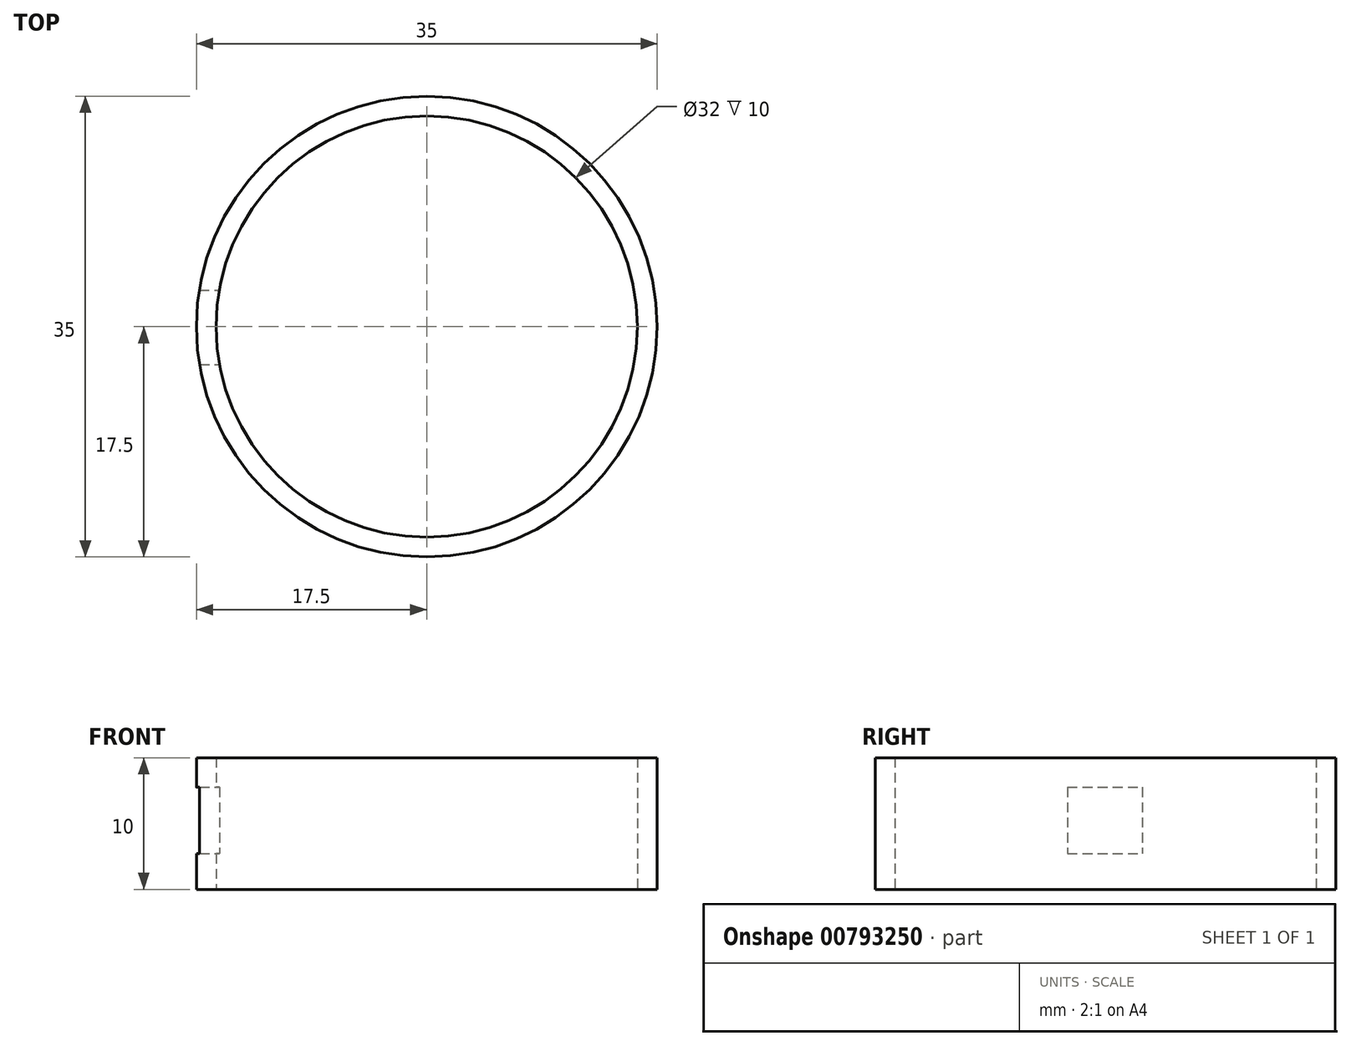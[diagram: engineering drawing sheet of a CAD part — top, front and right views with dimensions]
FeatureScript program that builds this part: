
annotation { "Feature Type Name" : "Feature", "Feature Type Description" : "" }
export const myFeature = defineFeature(function(context is Context, id is Id, definition is map)
    precondition{}
    {
        {
            var Q0;
            Q0=qCreatedBy(makeId("Top.planeOp"),FACE);
            var sketch = newSketch(context, id + "F0", { "sketchPlane" : qUnion([Q0])});
            skCircle(sketch, "E0", {"center": v(0, 0) * mm, "radius": 17.5 * mm});
            skCircle(sketch, "E1", {"center": v(0, 0) * mm, "radius": 16 * mm});
            skCircle(sketch, "E2", {"center": v(0, 0) * mm, "radius": 21.37 * mm});
            skCircle(sketch, "E3", {"center": v(0, 0) * mm, "radius": 12.63 * mm});
            skSolve(sketch);
        }
        {
            var Q0;
            Q0=makeQuery(id+"F0.imprint","IMPRINT",FACE,{"disambiguationData":[TD([[makeQuery(id+"F0.imprint","IMPRINT",EDGE,{"derivedFrom":sQuery(id+"F0.wireOp",EDGE,"E0")}),1.0]])]});
            extrude(context, id + "F1", {"entities" : qUnion([Q0]), "depth" : 10 * mm, "offsetDistance" : 25 * mm});
        }
        {
            var Q0;
            Q0=qCreatedBy(makeId("Right.planeOp"),FACE);
            var sketch = newSketch(context, id + "F2", { "sketchPlane" : qUnion([Q0])});
            skLineSegment(sketch, "E4.bottom", {"start": v(-2.9, 7.76) * mm, "end": v(2.78, 7.76) * mm});
            skLineSegment(sketch, "E4.top", {"start": v(-2.9, 2.7) * mm, "end": v(2.78, 2.7) * mm});
            skLineSegment(sketch, "E4.left", {"start": v(-2.9, 7.76) * mm, "end": v(-2.9, 2.7) * mm});
            skLineSegment(sketch, "E4.right", {"start": v(2.78, 7.76) * mm, "end": v(2.78, 2.7) * mm});
            skPoint(sketch, "E5.firstSnap0", {"position": v(2.78, 5.23) * mm});
            skLineSegment(sketch, "E5.bottom", {"start": v(7.45, 5.23) * mm, "end": v(-6.43, 5.23) * mm});
            skLineSegment(sketch, "E5.top", {"start": v(7.45, 4.22) * mm, "end": v(-6.43, 4.22) * mm});
            skLineSegment(sketch, "E5.left", {"start": v(7.45, 5.23) * mm, "end": v(7.45, 4.22) * mm});
            skLineSegment(sketch, "E5.right", {"start": v(-6.43, 5.23) * mm, "end": v(-6.43, 4.22) * mm});
            skSolve(sketch);
        }
        {
            var Q0;
            {var subQ0=sQuery(id+"F2.wireOp",EDGE,"E4.bottom");Q0=makeQuery(id+"F2.imprint","IMPRINT",FACE,{"disambiguationData":[TD([[makeQuery(id+"F2.imprint","IMPRINT",EDGE,{"derivedFrom":subQ0}),-1.0]])]});}
            var Q1;
            {var subQ0=sQuery(id+"F2.wireOp",EDGE,"E4.top");Q1=makeQuery(id+"F2.imprint","IMPRINT",FACE,{"disambiguationData":[TD([[makeQuery(id+"F2.imprint","IMPRINT",EDGE,{"derivedFrom":subQ0}),1.0]])]});}
            var Q2;
            {var subQ0=sQuery(id+"F2.wireOp",EDGE,"E5.bottom");var subQ1=sQuery(id+"F2.wireOp",EDGE,"E4.left");var subQ2=makeQuery(id+"F2.imprint","INTERSECT",VERTEX,{"derivedFrom":[subQ1,subQ0]});Q2=makeQuery(id+"F2.imprint","IMPRINT",FACE,{"disambiguationData":[TD([[makeQuery(id+"F2.imprint","IMPRINT",EDGE,{"disambiguationData":[TD([[subQ2,-1.0]])],"derivedFrom":subQ1}),1.0]])]});}
            extrude(context, id + "F3", {"entities" : qUnion([Q0, Q1, Q2]), "operationType" : NewBodyOperationType.REMOVE, "oppositeDirection" : true, "depth" : 25 * mm, "offsetDistance" : 25 * mm});
        }
    });
